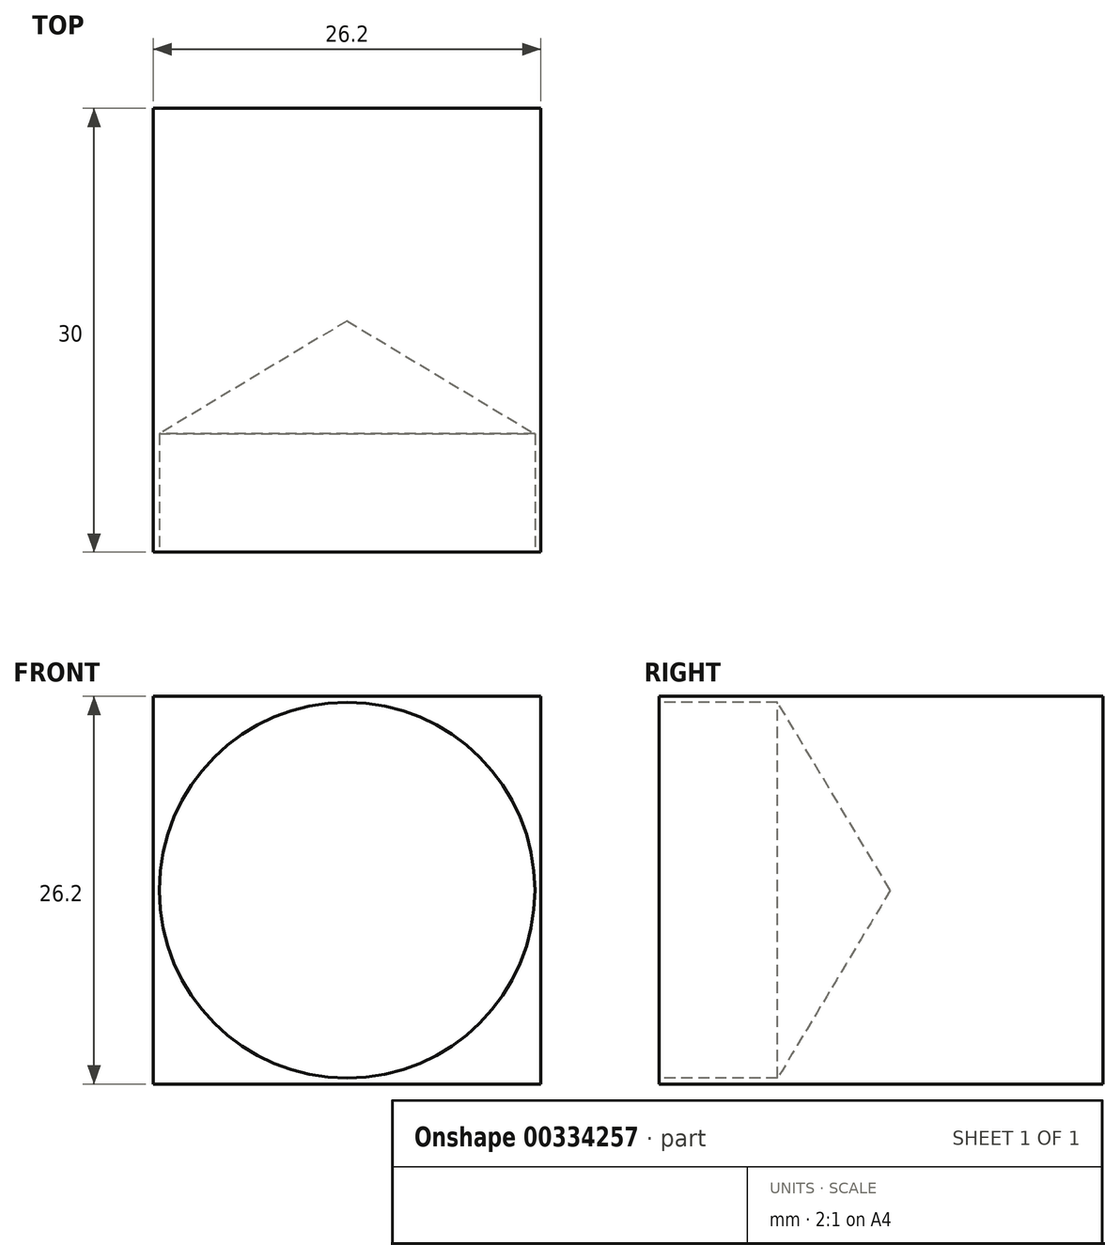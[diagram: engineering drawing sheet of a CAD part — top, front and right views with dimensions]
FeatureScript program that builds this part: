
annotation { "Feature Type Name" : "Feature", "Feature Type Description" : "" }
export const myFeature = defineFeature(function(context is Context, id is Id, definition is map)
    precondition{}
    {
        {
            var Q0;
            Q0=qCreatedBy(makeId("Front.planeOp"),FACE);
            var sketch = newSketch(context, id + "F0", { "sketchPlane" : qUnion([Q0])});
            skLineSegment(sketch, "E0.bottom", {"start": v(-13.1, 13.1) * mm, "end": v(13.1, 13.1) * mm});
            skLineSegment(sketch, "E0.top", {"start": v(-13.1, -13.1) * mm, "end": v(13.1, -13.1) * mm});
            skLineSegment(sketch, "E0.left", {"start": v(-13.1, 13.1) * mm, "end": v(-13.1, -13.1) * mm});
            skLineSegment(sketch, "E0.right", {"start": v(13.1, 13.1) * mm, "end": v(13.1, -13.1) * mm});
            skPoint(sketch, "E0.middle", {"position": v(0, 0) * mm});
            skSolve(sketch);
        }
        {
            var Q0;
            Q0=makeQuery(id+"F0.imprint","IMPRINT",FACE,{"disambiguationData":[TD([[makeQuery(id+"F0.imprint","IMPRINT",EDGE,{"derivedFrom":sQuery(id+"F0.wireOp",EDGE,"E0.bottom")}),-1.0]])]});
            extrude(context, id + "F1", {"entities" : qUnion([Q0]), "endBound" : BoundingType.SYMMETRIC, "depth" : 30 * mm});
        }
        {
            var Q0;
            Q0=makeQuery(id+"F1.opExtrude","CAP_FACE",FACE,{"disambiguationData":[OSD([sQuery(id+"F0.wireOp",EDGE,"E0.bottom"),sQuery(id+"F0.wireOp",EDGE,"E0.top"),sQuery(id+"F0.wireOp",EDGE,"E0.left"),sQuery(id+"F0.wireOp",EDGE,"E0.right")])],"isStart":false});
            var sketch = newSketch(context, id + "F2", { "sketchPlane" : qUnion([Q0])});
            skPoint(sketch, "E1", {"position": v(0, 0) * mm});
            skSolve(sketch);
        }
        {
            var Q0;
            Q0=sQuery(id+"F2.wireOp",VERTEX,"E1");
            var Q1;
            Q1=makeQuery(id+"F1.opExtrude","SWEPT_BODY",BODY,{"disambiguationData":[OSD([sQuery(id+"F0.wireOp",EDGE,"E0.bottom"),sQuery(id+"F0.wireOp",EDGE,"E0.top"),sQuery(id+"F0.wireOp",EDGE,"E0.left"),sQuery(id+"F0.wireOp",EDGE,"E0.right")])]});
            hole(context, id + "F3", {"style" : HoleStyle.SIMPLE, "endStyle" : HoleEndStyle.BLIND, "holeDiameter" : 25.4 * mm, "holeDepth" : 8 * mm, "tappedDepth" : 12 * mm, "tapClearance" : 3, "locations" : qUnion([Q0]), "scope" : qUnion([Q1])});
        }
    });
